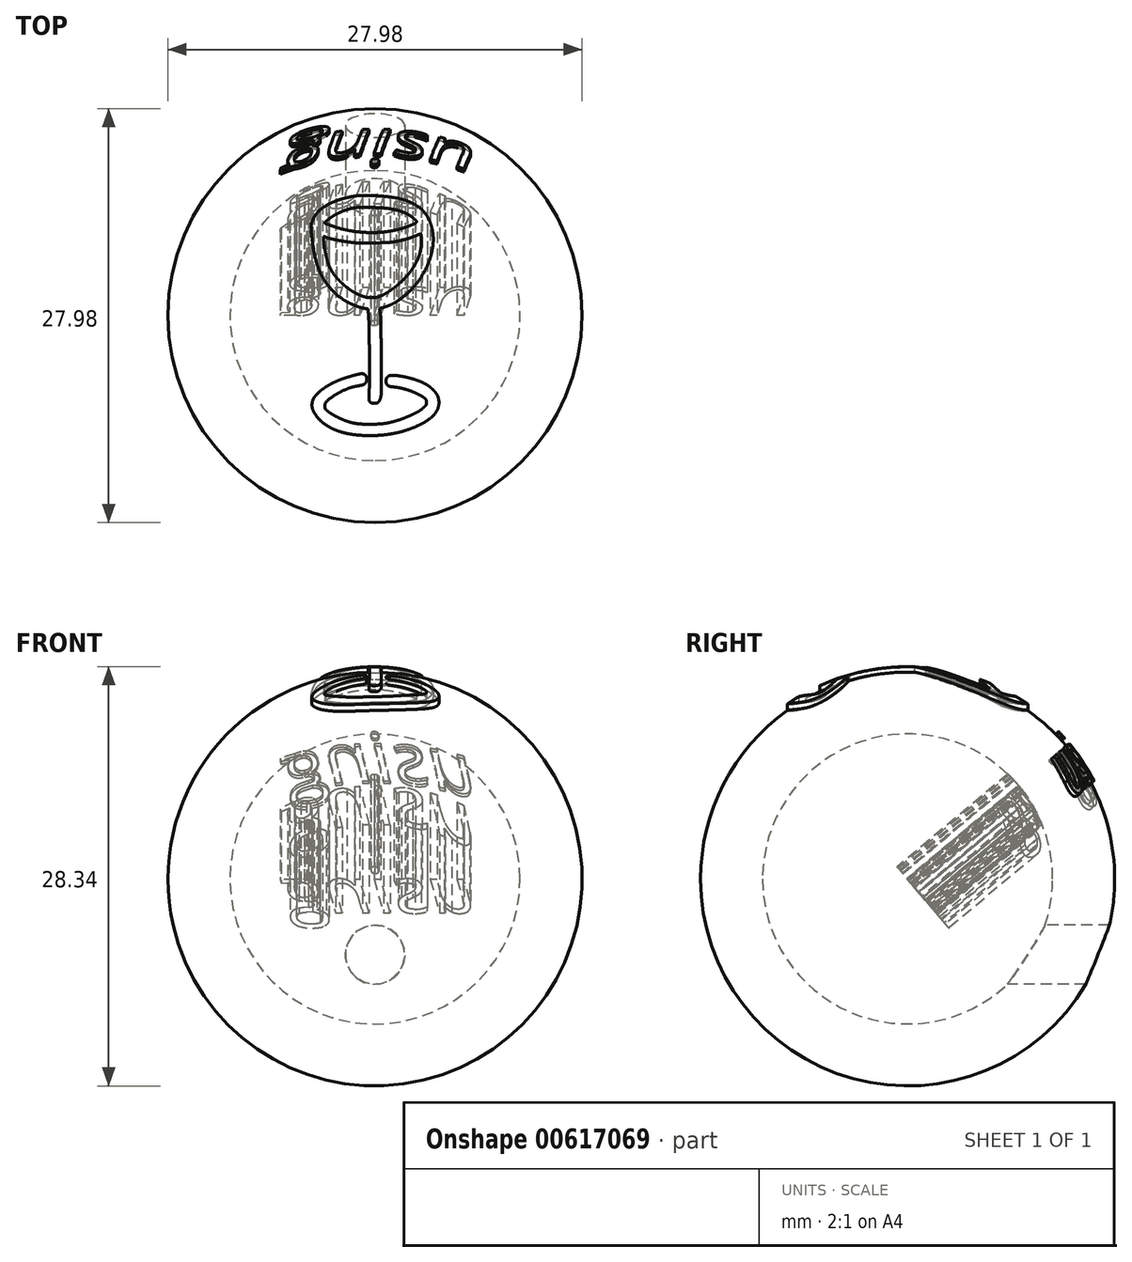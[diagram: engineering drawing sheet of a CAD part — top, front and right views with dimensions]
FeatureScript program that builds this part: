
annotation { "Feature Type Name" : "Feature", "Feature Type Description" : "" }
export const myFeature = defineFeature(function(context is Context, id is Id, definition is map)
    precondition{}
    {
        {
            var Q0;
            Q0=qCreatedBy(makeId("Top.planeOp"),FACE);
            var sketch = newSketch(context, id + "F0", { "sketchPlane" : qUnion([Q0])});
            skLineSegment(sketch, "E0", {"start": v(0, -10) * mm, "end": v(0, 10) * mm});
            skArc(sketch, "E1", {"start": v(0, 10) * mm, "mid": v(-10, 0) * mm, "end": v(0, -10) * mm});
            skSolve(sketch);
        }
        {
            var Q0;
            {var subQ0=sQuery(id+"F0.wireOp",EDGE,"E1");Q0=makeQuery(id+"F0.imprint","IMPRINT",FACE,{"disambiguationData":[TD([[makeQuery(id+"F0.imprint","IMPRINT",EDGE,{"derivedFrom":subQ0}),1.0]])]});}
            var Q1;
            Q1=sQuery(id+"F0.wireOp",EDGE,"E0");
            revolve(context, id + "F1", {"entities" : qUnion([Q0]), "axis" : qUnion([Q1]), "revolveType" : RevolveType.FULL});
        }
        {
            var Q0;
            Q0=makeQuery(id+"F1.opRevolve","SWEPT_BODY",BODY,{"disambiguationData":[OSD([sQuery(id+"F0.wireOp",EDGE,"E0"),sQuery(id+"F0.wireOp",EDGE,"E1")])]});
            var Q1;
            Q1=sQuery(id+"F0.wireOp",VERTEX,"NPe4G0ez-t7S9-9isL-QO5v-uuJu600mHcIT.center");
            var Q2;
            Q2=sQuery(id+"F0.wireOp",VERTEX,"E1.center");
            transform(context, id + "F2", {"entities" : qUnion([Q0]), "transformType" : TransformType.SCALE_UNIFORMLY, "scale" : 33.3, "scalePoint" : qUnion([Q2]), "makeCopy" : false});
        }
        {
            var Q0;
            Q0=qCreatedBy(makeId("Top.planeOp"),FACE);
            var sketch = newSketch(context, id + "F3", { "sketchPlane" : qUnion([Q0])});
            skArc(sketch, "E2", {"start": v(-28, 192.81) * mm, "mid": v(-31.38, 192.4) * mm, "end": v(-34.76, 191.86) * mm});
            skArc(sketch, "E3", {"start": v(-34.76, 191.86) * mm, "mid": v(-38.6, 191.14) * mm, "end": v(-42.43, 190.34) * mm});
            skArc(sketch, "E4", {"start": v(-42.43, 190.34) * mm, "mid": v(-46.3, 189.44) * mm, "end": v(-50.14, 188.46) * mm});
            skArc(sketch, "E5", {"start": v(-50.14, 188.46) * mm, "mid": v(-53.62, 187.47) * mm, "end": v(-57.07, 186.38) * mm});
            skArc(sketch, "E6", {"start": v(-57.07, 186.38) * mm, "mid": v(-64.8, 183.56) * mm, "end": v(-72.35, 180.29) * mm});
            skArc(sketch, "E7", {"start": v(-72.35, 180.29) * mm, "mid": v(-78.57, 177) * mm, "end": v(-84.46, 173.13) * mm});
            skArc(sketch, "E8", {"start": v(-84.46, 173.13) * mm, "mid": v(-89.14, 169.3) * mm, "end": v(-93.37, 164.97) * mm});
            skArc(sketch, "E9", {"start": v(-93.37, 164.97) * mm, "mid": v(-96.59, 160.63) * mm, "end": v(-99.08, 155.83) * mm});
            skArc(sketch, "E10", {"start": v(-99.08, 155.83) * mm, "mid": v(-99.5, 154.83) * mm, "end": v(-99.94, 153.82) * mm});
            skArc(sketch, "E11", {"start": v(-99.94, 153.82) * mm, "mid": v(-100.4, 152.79) * mm, "end": v(-100.85, 151.75) * mm});
            skArc(sketch, "E12", {"start": v(-100.85, 151.75) * mm, "mid": v(-101.26, 150.84) * mm, "end": v(-101.67, 149.92) * mm});
            skArc(sketch, "E13", {"start": v(-101.67, 149.92) * mm, "mid": v(-101.95, 149.32) * mm, "end": v(-102.24, 148.73) * mm});
            skArc(sketch, "E14", {"start": v(-102.24, 148.73) * mm, "mid": v(-102.57, 147.87) * mm, "end": v(-102.73, 146.96) * mm});
            skArc(sketch, "E15", {"start": v(-102.73, 146.96) * mm, "mid": v(-102.82, 145.41) * mm, "end": v(-102.85, 143.86) * mm});
            skArc(sketch, "E16", {"start": v(-102.85, 143.86) * mm, "mid": v(-102.8, 141.6) * mm, "end": v(-102.69, 139.34) * mm});
            skArc(sketch, "E17", {"start": v(-102.69, 139.34) * mm, "mid": v(-102.44, 135.94) * mm, "end": v(-102.17, 132.54) * mm});
            skArc(sketch, "E18", {"start": v(-102.17, 132.54) * mm, "mid": v(-100.04, 114.16) * mm, "end": v(-96.8, 95.94) * mm});
            skArc(sketch, "E19", {"start": v(-96.8, 95.94) * mm, "mid": v(-92.94, 81.56) * mm, "end": v(-87.47, 67.71) * mm});
            skArc(sketch, "E20", {"start": v(-87.47, 67.71) * mm, "mid": v(-81.13, 56.12) * mm, "end": v(-73.3, 45.49) * mm});
            skArc(sketch, "E21", {"start": v(-73.3, 45.49) * mm, "mid": v(-63.92, 35.71) * mm, "end": v(-53.4, 27.18) * mm});
            skArc(sketch, "E22", {"start": v(-53.4, 27.18) * mm, "mid": v(-49.24, 24.41) * mm, "end": v(-44.9, 21.92) * mm});
            skArc(sketch, "E23", {"start": v(-44.9, 21.92) * mm, "mid": v(-39.88, 19.4) * mm, "end": v(-34.74, 17.1) * mm});
            skArc(sketch, "E24", {"start": v(-34.74, 17.1) * mm, "mid": v(-29.55, 15.07) * mm, "end": v(-24.28, 13.28) * mm});
            skArc(sketch, "E25", {"start": v(-24.28, 13.28) * mm, "mid": v(-19.62, 12) * mm, "end": v(-14.89, 11.06) * mm});
            skLineSegment(sketch, "E26", {"start": v(-14.89, 11.06) * mm, "end": v(-11.28, 10.47) * mm});
            skLineSegment(sketch, "E27", {"start": v(-11.28, 10.47) * mm, "end": v(-10.56, 2.24) * mm});
            skArc(sketch, "E28", {"start": v(-10.56, 2.24) * mm, "mid": v(-9.95, -6.44) * mm, "end": v(-9.64, -15.14) * mm});
            skArc(sketch, "E29", {"start": v(-9.64, -15.14) * mm, "mid": v(-9.3, -35.9) * mm, "end": v(-9.02, -56.67) * mm});
            skArc(sketch, "E30", {"start": v(-9.02, -56.67) * mm, "mid": v(-8.82, -77.32) * mm, "end": v(-8.7, -97.97) * mm});
            skArc(sketch, "E31", {"start": v(-8.7, -97.97) * mm, "mid": v(-8.8, -108.17) * mm, "end": v(-9.18, -118.37) * mm});
            skArc(sketch, "E32", {"start": v(-9.18, -118.37) * mm, "mid": v(-9.47, -124.4) * mm, "end": v(-9.74, -130.44) * mm});
            skArc(sketch, "E33", {"start": v(-9.74, -130.44) * mm, "mid": v(-9.78, -132.57) * mm, "end": v(-9.7, -134.7) * mm});
            skArc(sketch, "E34", {"start": v(-9.7, -134.7) * mm, "mid": v(-9.52, -135.94) * mm, "end": v(-9.15, -137.13) * mm});
            skArc(sketch, "E35", {"start": v(-9.15, -137.13) * mm, "mid": v(-8.6, -138.18) * mm, "end": v(-7.87, -139.12) * mm});
            skArc(sketch, "E36", {"start": v(-7.87, -139.12) * mm, "mid": v(-7.27, -139.7) * mm, "end": v(-6.62, -140.22) * mm});
            skArc(sketch, "E37", {"start": v(-6.62, -140.22) * mm, "mid": v(-5.96, -140.63) * mm, "end": v(-5.26, -140.95) * mm});
            skArc(sketch, "E38", {"start": v(-5.26, -140.95) * mm, "mid": v(-4.48, -141.2) * mm, "end": v(-3.68, -141.36) * mm});
            skArc(sketch, "E39", {"start": v(-3.68, -141.36) * mm, "mid": v(-2.72, -141.46) * mm, "end": v(-1.75, -141.5) * mm});
            skArc(sketch, "E40", {"start": v(-1.75, -141.5) * mm, "mid": v(0, -141.42) * mm, "end": v(1.72, -141.18) * mm});
            skArc(sketch, "E41", {"start": v(1.72, -141.18) * mm, "mid": v(3.04, -140.82) * mm, "end": v(4.26, -140.22) * mm});
            skArc(sketch, "E42", {"start": v(4.26, -140.22) * mm, "mid": v(5.31, -139.43) * mm, "end": v(6.2, -138.45) * mm});
            skArc(sketch, "E43", {"start": v(6.2, -138.45) * mm, "mid": v(7.08, -137.1) * mm, "end": v(7.82, -135.66) * mm});
            skArc(sketch, "E44", {"start": v(7.82, -135.66) * mm, "mid": v(9.39, -130.88) * mm, "end": v(9.93, -125.87) * mm});
            skArc(sketch, "E45", {"start": v(9.93, -125.87) * mm, "mid": v(9.97, -95.78) * mm, "end": v(9.93, -65.68) * mm});
            skArc(sketch, "E46", {"start": v(9.93, -65.68) * mm, "mid": v(9.77, -36.7) * mm, "end": v(9.47, -7.73) * mm});
            skArc(sketch, "E47", {"start": v(9.47, -7.73) * mm, "mid": v(8.9, 0.7) * mm, "end": v(7.4, 9) * mm});
            skArc(sketch, "E48", {"start": v(7.4, 9) * mm, "mid": v(7.35, 9.57) * mm, "end": v(7.47, 10.13) * mm});
            skArc(sketch, "E49", {"start": v(7.47, 10.13) * mm, "mid": v(7.75, 10.61) * mm, "end": v(8.17, 10.99) * mm});
            skArc(sketch, "E50", {"start": v(8.17, 10.99) * mm, "mid": v(8.98, 11.43) * mm, "end": v(9.85, 11.77) * mm});
            skArc(sketch, "E51", {"start": v(9.85, 11.77) * mm, "mid": v(11.67, 12.35) * mm, "end": v(13.5, 12.9) * mm});
            skArc(sketch, "E52", {"start": v(13.5, 12.9) * mm, "mid": v(25.53, 17.38) * mm, "end": v(36.7, 23.67) * mm});
            skArc(sketch, "E53", {"start": v(36.7, 23.67) * mm, "mid": v(48.2, 32.34) * mm, "end": v(58.64, 42.23) * mm});
            skArc(sketch, "E54", {"start": v(58.64, 42.23) * mm, "mid": v(68.36, 53.67) * mm, "end": v(76.8, 66.08) * mm});
            skArc(sketch, "E55", {"start": v(76.8, 66.08) * mm, "mid": v(83.57, 78.94) * mm, "end": v(88.8, 92.5) * mm});
            skArc(sketch, "E56", {"start": v(88.8, 92.5) * mm, "mid": v(91.23, 101.41) * mm, "end": v(92.9, 110.5) * mm});
            skArc(sketch, "E57", {"start": v(92.9, 110.5) * mm, "mid": v(93.67, 119.1) * mm, "end": v(93.55, 127.73) * mm});
            skArc(sketch, "E58", {"start": v(93.55, 127.73) * mm, "mid": v(92.56, 135.93) * mm, "end": v(90.68, 143.97) * mm});
            skArc(sketch, "E59", {"start": v(90.68, 143.97) * mm, "mid": v(87.96, 151.66) * mm, "end": v(84.4, 159) * mm});
            skArc(sketch, "E60", {"start": v(84.4, 159) * mm, "mid": v(80.6, 164.75) * mm, "end": v(75.97, 169.86) * mm});
            skArc(sketch, "E61", {"start": v(75.97, 169.86) * mm, "mid": v(70.26, 174.63) * mm, "end": v(64.02, 178.68) * mm});
            skArc(sketch, "E62", {"start": v(64.02, 178.68) * mm, "mid": v(56.48, 182.45) * mm, "end": v(48.6, 185.4) * mm});
            skArc(sketch, "E63", {"start": v(48.6, 185.4) * mm, "mid": v(39.26, 188) * mm, "end": v(29.76, 189.95) * mm});
            skArc(sketch, "E64", {"start": v(29.76, 189.95) * mm, "mid": v(23.24, 190.92) * mm, "end": v(16.69, 191.62) * mm});
            skArc(sketch, "E65", {"start": v(16.69, 191.62) * mm, "mid": v(8.13, 192.28) * mm, "end": v(-0.44, 192.79) * mm});
            skArc(sketch, "E66", {"start": v(-0.44, 192.79) * mm, "mid": v(-8.76, 193.13) * mm, "end": v(-17.1, 193.32) * mm});
            skArc(sketch, "E67", {"start": v(-17.1, 193.32) * mm, "mid": v(-22.55, 193.23) * mm, "end": v(-28, 192.81) * mm});
            skArc(sketch, "E68", {"start": v(23, 172) * mm, "mid": v(27.27, 171.24) * mm, "end": v(31.52, 170.4) * mm});
            skArc(sketch, "E69", {"start": v(31.52, 170.4) * mm, "mid": v(34.9, 169.63) * mm, "end": v(38.25, 168.73) * mm});
            skArc(sketch, "E70", {"start": v(38.25, 168.73) * mm, "mid": v(41.28, 167.77) * mm, "end": v(44.27, 166.68) * mm});
            skArc(sketch, "E71", {"start": v(44.27, 166.68) * mm, "mid": v(47.43, 165.38) * mm, "end": v(50.56, 163.97) * mm});
            skArc(sketch, "E72", {"start": v(50.56, 163.97) * mm, "mid": v(53.44, 162.47) * mm, "end": v(56.2, 160.78) * mm});
            skArc(sketch, "E73", {"start": v(56.2, 160.78) * mm, "mid": v(59.05, 158.78) * mm, "end": v(61.78, 156.62) * mm});
            skArc(sketch, "E74", {"start": v(61.78, 156.62) * mm, "mid": v(64.08, 154.6) * mm, "end": v(66.28, 152.48) * mm});
            skArc(sketch, "E75", {"start": v(66.28, 152.48) * mm, "mid": v(66.84, 151.48) * mm, "end": v(66.79, 150.33) * mm});
            skArc(sketch, "E76", {"start": v(66.79, 150.33) * mm, "mid": v(66.12, 149.19) * mm, "end": v(65.05, 148.41) * mm});
            skArc(sketch, "E77", {"start": v(65.05, 148.41) * mm, "mid": v(60.8, 146.55) * mm, "end": v(56.5, 144.76) * mm});
            skArc(sketch, "E78", {"start": v(56.5, 144.76) * mm, "mid": v(51.74, 142.91) * mm, "end": v(46.93, 141.22) * mm});
            skArc(sketch, "E79", {"start": v(46.93, 141.22) * mm, "mid": v(42.34, 139.79) * mm, "end": v(37.7, 138.53) * mm});
            skArc(sketch, "E80", {"start": v(37.7, 138.53) * mm, "mid": v(24.83, 135.84) * mm, "end": v(11.79, 134.2) * mm});
            skArc(sketch, "E81", {"start": v(11.79, 134.2) * mm, "mid": v(-2.07, 133.48) * mm, "end": v(-15.94, 133.71) * mm});
            skArc(sketch, "E82", {"start": v(-15.94, 133.71) * mm, "mid": v(-29.73, 134.9) * mm, "end": v(-43.4, 137.01) * mm});
            skArc(sketch, "E83", {"start": v(-43.4, 137.01) * mm, "mid": v(-56.09, 139.97) * mm, "end": v(-68.5, 143.96) * mm});
            skArc(sketch, "E84", {"start": v(-68.5, 143.96) * mm, "mid": v(-70.45, 144.68) * mm, "end": v(-72.41, 145.4) * mm});
            skArc(sketch, "E85", {"start": v(-72.41, 145.4) * mm, "mid": v(-74.17, 146.03) * mm, "end": v(-75.92, 146.67) * mm});
            skArc(sketch, "E86", {"start": v(-75.92, 146.67) * mm, "mid": v(-77.4, 147.2) * mm, "end": v(-78.88, 147.74) * mm});
            skArc(sketch, "E87", {"start": v(-78.88, 147.74) * mm, "mid": v(-79.3, 147.9) * mm, "end": v(-79.74, 148.04) * mm});
            skArc(sketch, "E88", {"start": v(-79.74, 148.04) * mm, "mid": v(-80.25, 148.32) * mm, "end": v(-80.62, 148.77) * mm});
            skArc(sketch, "E89", {"start": v(-80.62, 148.77) * mm, "mid": v(-80.74, 149.28) * mm, "end": v(-80.58, 149.77) * mm});
            skArc(sketch, "E90", {"start": v(-80.58, 149.77) * mm, "mid": v(-79.94, 150.6) * mm, "end": v(-79.2, 151.33) * mm});
            skArc(sketch, "E91", {"start": v(-79.2, 151.33) * mm, "mid": v(-77.48, 152.74) * mm, "end": v(-75.74, 154.13) * mm});
            skArc(sketch, "E92", {"start": v(-75.74, 154.13) * mm, "mid": v(-70.76, 157.76) * mm, "end": v(-65.57, 161.08) * mm});
            skArc(sketch, "E93", {"start": v(-65.57, 161.08) * mm, "mid": v(-60.08, 164.12) * mm, "end": v(-54.43, 166.82) * mm});
            skArc(sketch, "E94", {"start": v(-54.43, 166.82) * mm, "mid": v(-48.77, 169.12) * mm, "end": v(-43, 171.06) * mm});
            skArc(sketch, "E95", {"start": v(-43, 171.06) * mm, "mid": v(-37.5, 172.49) * mm, "end": v(-31.93, 173.5) * mm});
            skArc(sketch, "E96", {"start": v(-31.93, 173.5) * mm, "mid": v(-27.17, 174) * mm, "end": v(-22.38, 174.16) * mm});
            skArc(sketch, "E97", {"start": v(-22.38, 174.16) * mm, "mid": v(-13.79, 174.1) * mm, "end": v(-5.2, 173.93) * mm});
            skArc(sketch, "E98", {"start": v(-5.2, 173.93) * mm, "mid": v(3.46, 173.63) * mm, "end": v(12.1, 173.2) * mm});
            skArc(sketch, "E99", {"start": v(12.1, 173.2) * mm, "mid": v(17.57, 172.75) * mm, "end": v(23, 172) * mm});
            skArc(sketch, "E100", {"start": v(74.45, 118.91) * mm, "mid": v(74.2, 112.9) * mm, "end": v(73.54, 106.92) * mm});
            skArc(sketch, "E101", {"start": v(73.54, 106.92) * mm, "mid": v(72.47, 101.46) * mm, "end": v(70.92, 96.12) * mm});
            skArc(sketch, "E102", {"start": v(70.92, 96.12) * mm, "mid": v(68.79, 90.64) * mm, "end": v(66.2, 85.35) * mm});
            skArc(sketch, "E103", {"start": v(66.2, 85.35) * mm, "mid": v(62.73, 79.3) * mm, "end": v(58.94, 73.4) * mm});
            skArc(sketch, "E104", {"start": v(58.94, 73.4) * mm, "mid": v(54.72, 67.67) * mm, "end": v(50.07, 62.26) * mm});
            skArc(sketch, "E105", {"start": v(50.07, 62.26) * mm, "mid": v(44.37, 56.43) * mm, "end": v(38.38, 50.9) * mm});
            skArc(sketch, "E106", {"start": v(38.38, 50.9) * mm, "mid": v(32.1, 45.67) * mm, "end": v(25.56, 40.76) * mm});
            skArc(sketch, "E107", {"start": v(25.56, 40.76) * mm, "mid": v(19.56, 36.81) * mm, "end": v(13.27, 33.33) * mm});
            skArc(sketch, "E108", {"start": v(13.27, 33.33) * mm, "mid": v(10.86, 32.14) * mm, "end": v(8.43, 31.02) * mm});
            skArc(sketch, "E109", {"start": v(8.43, 31.02) * mm, "mid": v(6.75, 30.34) * mm, "end": v(5.03, 29.79) * mm});
            skArc(sketch, "E110", {"start": v(5.03, 29.79) * mm, "mid": v(3.33, 29.38) * mm, "end": v(1.6, 29.12) * mm});
            skArc(sketch, "E111", {"start": v(1.6, 29.12) * mm, "mid": v(-0.81, 28.88) * mm, "end": v(-3.23, 28.72) * mm});
            skArc(sketch, "E112", {"start": v(-3.23, 28.72) * mm, "mid": v(-5.59, 28.63) * mm, "end": v(-7.95, 28.6) * mm});
            skArc(sketch, "E113", {"start": v(-7.95, 28.6) * mm, "mid": v(-9.7, 28.66) * mm, "end": v(-11.43, 28.84) * mm});
            skArc(sketch, "E114", {"start": v(-11.43, 28.84) * mm, "mid": v(-13.15, 29.14) * mm, "end": v(-14.86, 29.55) * mm});
            skArc(sketch, "E115", {"start": v(-14.86, 29.55) * mm, "mid": v(-17.14, 30.22) * mm, "end": v(-19.4, 30.94) * mm});
            skArc(sketch, "E116", {"start": v(-19.4, 30.94) * mm, "mid": v(-24.3, 32.77) * mm, "end": v(-29.04, 34.94) * mm});
            skArc(sketch, "E117", {"start": v(-29.04, 34.94) * mm, "mid": v(-33.85, 37.5) * mm, "end": v(-38.48, 40.37) * mm});
            skArc(sketch, "E118", {"start": v(-38.48, 40.37) * mm, "mid": v(-43.29, 43.72) * mm, "end": v(-47.9, 47.34) * mm});
            skArc(sketch, "E119", {"start": v(-47.9, 47.34) * mm, "mid": v(-52.76, 51.57) * mm, "end": v(-57.44, 56) * mm});
            skArc(sketch, "E120", {"start": v(-57.44, 56) * mm, "mid": v(-62.23, 61.17) * mm, "end": v(-66.53, 66.76) * mm});
            skArc(sketch, "E121", {"start": v(-66.53, 66.76) * mm, "mid": v(-70.15, 72.57) * mm, "end": v(-73.17, 78.7) * mm});
            skArc(sketch, "E122", {"start": v(-73.17, 78.7) * mm, "mid": v(-75.9, 85.84) * mm, "end": v(-77.98, 93.19) * mm});
            skArc(sketch, "E123", {"start": v(-77.98, 93.19) * mm, "mid": v(-79.95, 102.45) * mm, "end": v(-81.5, 111.79) * mm});
            skArc(sketch, "E124", {"start": v(-81.5, 111.79) * mm, "mid": v(-81.79, 113.84) * mm, "end": v(-82.06, 115.9) * mm});
            skArc(sketch, "E125", {"start": v(-82.06, 115.9) * mm, "mid": v(-82.3, 117.84) * mm, "end": v(-82.53, 119.8) * mm});
            skArc(sketch, "E126", {"start": v(-82.53, 119.8) * mm, "mid": v(-82.72, 121.44) * mm, "end": v(-82.89, 123.1) * mm});
            skArc(sketch, "E127", {"start": v(-82.89, 123.1) * mm, "mid": v(-82.95, 123.9) * mm, "end": v(-82.97, 124.7) * mm});
            skLineSegment(sketch, "E128", {"start": v(-82.97, 124.7) * mm, "end": v(-83, 127.4) * mm});
            skLineSegment(sketch, "E129", {"start": v(-83, 127.4) * mm, "end": v(-77.24, 125.41) * mm});
            skArc(sketch, "E130", {"start": v(-77.24, 125.41) * mm, "mid": v(-73.46, 124.22) * mm, "end": v(-69.61, 123.22) * mm});
            skArc(sketch, "E131", {"start": v(-69.61, 123.22) * mm, "mid": v(-64.09, 122) * mm, "end": v(-58.54, 120.88) * mm});
            skArc(sketch, "E132", {"start": v(-58.54, 120.88) * mm, "mid": v(-52.55, 119.8) * mm, "end": v(-46.55, 118.82) * mm});
            skArc(sketch, "E133", {"start": v(-46.55, 118.82) * mm, "mid": v(-41.1, 118.06) * mm, "end": v(-35.66, 117.44) * mm});
            skArc(sketch, "E134", {"start": v(-35.66, 117.44) * mm, "mid": v(-28.26, 116.87) * mm, "end": v(-20.84, 116.63) * mm});
            skArc(sketch, "E135", {"start": v(-20.84, 116.63) * mm, "mid": v(-10.4, 116.6) * mm, "end": v(0.05, 116.76) * mm});
            skArc(sketch, "E136", {"start": v(0.05, 116.76) * mm, "mid": v(10.3, 117.07) * mm, "end": v(20.54, 117.54) * mm});
            skArc(sketch, "E137", {"start": v(20.54, 117.54) * mm, "mid": v(26.8, 118.08) * mm, "end": v(33, 119) * mm});
            skArc(sketch, "E138", {"start": v(33, 119) * mm, "mid": v(37.48, 119.88) * mm, "end": v(41.92, 120.86) * mm});
            skArc(sketch, "E139", {"start": v(41.92, 120.86) * mm, "mid": v(46.33, 121.94) * mm, "end": v(50.71, 123.15) * mm});
            skArc(sketch, "E140", {"start": v(50.71, 123.15) * mm, "mid": v(54.81, 124.38) * mm, "end": v(58.87, 125.73) * mm});
            skArc(sketch, "E141", {"start": v(58.87, 125.73) * mm, "mid": v(62.4, 127.02) * mm, "end": v(65.87, 128.45) * mm});
            skArc(sketch, "E142", {"start": v(65.87, 128.45) * mm, "mid": v(67.17, 129.01) * mm, "end": v(68.48, 129.54) * mm});
            skArc(sketch, "E143", {"start": v(68.48, 129.54) * mm, "mid": v(69.66, 130) * mm, "end": v(70.85, 130.42) * mm});
            skArc(sketch, "E144", {"start": v(70.85, 130.42) * mm, "mid": v(71.84, 130.75) * mm, "end": v(72.84, 131.07) * mm});
            skArc(sketch, "E145", {"start": v(72.84, 131.07) * mm, "mid": v(73.17, 131.13) * mm, "end": v(73.5, 131.09) * mm});
            skArc(sketch, "E146", {"start": v(73.5, 131.09) * mm, "mid": v(73.8, 130.9) * mm, "end": v(73.94, 130.6) * mm});
            skArc(sketch, "E147", {"start": v(73.94, 130.6) * mm, "mid": v(74.09, 129.1) * mm, "end": v(74.22, 127.62) * mm});
            skArc(sketch, "E148", {"start": v(74.22, 127.62) * mm, "mid": v(74.34, 125.7) * mm, "end": v(74.4, 123.79) * mm});
            skArc(sketch, "E149", {"start": v(74.4, 123.79) * mm, "mid": v(74.45, 121.35) * mm, "end": v(74.45, 118.91) * mm});
            skArc(sketch, "E150", {"start": v(-34.65, -96.5) * mm, "mid": v(-43.47, -99) * mm, "end": v(-52.16, -101.92) * mm});
            skArc(sketch, "E151", {"start": v(-52.16, -101.92) * mm, "mid": v(-60, -105) * mm, "end": v(-67.65, -108.52) * mm});
            skArc(sketch, "E152", {"start": v(-67.65, -108.52) * mm, "mid": v(-74.33, -112.1) * mm, "end": v(-80.77, -116.1) * mm});
            skArc(sketch, "E153", {"start": v(-80.77, -116.1) * mm, "mid": v(-86.14, -120.06) * mm, "end": v(-91.13, -124.5) * mm});
            skArc(sketch, "E154", {"start": v(-91.13, -124.5) * mm, "mid": v(-93.26, -126.63) * mm, "end": v(-95.35, -128.8) * mm});
            skArc(sketch, "E155", {"start": v(-95.35, -128.8) * mm, "mid": v(-96.6, -130.2) * mm, "end": v(-97.73, -131.7) * mm});
            skArc(sketch, "E156", {"start": v(-97.73, -131.7) * mm, "mid": v(-98.56, -133.01) * mm, "end": v(-99.25, -134.4) * mm});
            skArc(sketch, "E157", {"start": v(-99.25, -134.4) * mm, "mid": v(-99.92, -136.08) * mm, "end": v(-100.48, -137.8) * mm});
            skArc(sketch, "E158", {"start": v(-100.48, -137.8) * mm, "mid": v(-101.1, -140.5) * mm, "end": v(-101.43, -143.24) * mm});
            skArc(sketch, "E159", {"start": v(-101.43, -143.24) * mm, "mid": v(-101.41, -145.8) * mm, "end": v(-101.04, -148.34) * mm});
            skArc(sketch, "E160", {"start": v(-101.04, -148.34) * mm, "mid": v(-100.3, -151.03) * mm, "end": v(-99.22, -153.6) * mm});
            skArc(sketch, "E161", {"start": v(-99.22, -153.6) * mm, "mid": v(-97.61, -156.62) * mm, "end": v(-95.8, -159.53) * mm});
            skArc(sketch, "E162", {"start": v(-95.8, -159.53) * mm, "mid": v(-89.92, -166.94) * mm, "end": v(-82.9, -173.28) * mm});
            skArc(sketch, "E163", {"start": v(-82.9, -173.28) * mm, "mid": v(-74.32, -179.02) * mm, "end": v(-65.07, -183.62) * mm});
            skArc(sketch, "E164", {"start": v(-65.07, -183.62) * mm, "mid": v(-54.02, -187.58) * mm, "end": v(-42.6, -190.32) * mm});
            skArc(sketch, "E165", {"start": v(-42.6, -190.32) * mm, "mid": v(-29.29, -192.24) * mm, "end": v(-15.88, -193.2) * mm});
            skArc(sketch, "E166", {"start": v(-15.88, -193.2) * mm, "mid": v(-3.6, -193.28) * mm, "end": v(8.67, -192.7) * mm});
            skArc(sketch, "E167", {"start": v(8.67, -192.7) * mm, "mid": v(20.3, -191.45) * mm, "end": v(31.83, -189.47) * mm});
            skArc(sketch, "E168", {"start": v(31.83, -189.47) * mm, "mid": v(42.82, -186.85) * mm, "end": v(53.62, -183.51) * mm});
            skArc(sketch, "E169", {"start": v(53.62, -183.51) * mm, "mid": v(64, -179.52) * mm, "end": v(74.07, -174.83) * mm});
            skArc(sketch, "E170", {"start": v(74.07, -174.83) * mm, "mid": v(81.9, -170.36) * mm, "end": v(89.25, -165.16) * mm});
            skArc(sketch, "E171", {"start": v(89.25, -165.16) * mm, "mid": v(94.55, -160.17) * mm, "end": v(98.88, -154.31) * mm});
            skArc(sketch, "E172", {"start": v(98.88, -154.31) * mm, "mid": v(101.48, -148.67) * mm, "end": v(102.73, -142.58) * mm});
            skArc(sketch, "E173", {"start": v(102.73, -142.58) * mm, "mid": v(102.6, -136.36) * mm, "end": v(101.06, -130.32) * mm});
            skArc(sketch, "E174", {"start": v(101.06, -130.32) * mm, "mid": v(99.8, -127.56) * mm, "end": v(98.15, -125) * mm});
            skArc(sketch, "E175", {"start": v(98.15, -125) * mm, "mid": v(95.8, -122.07) * mm, "end": v(93.23, -119.32) * mm});
            skArc(sketch, "E176", {"start": v(93.23, -119.32) * mm, "mid": v(90.25, -116.55) * mm, "end": v(87.08, -114) * mm});
            skArc(sketch, "E177", {"start": v(87.08, -114) * mm, "mid": v(83.81, -111.76) * mm, "end": v(80.39, -109.77) * mm});
            skArc(sketch, "E178", {"start": v(80.39, -109.77) * mm, "mid": v(74.8, -107.06) * mm, "end": v(69.03, -104.76) * mm});
            skArc(sketch, "E179", {"start": v(69.03, -104.76) * mm, "mid": v(62.06, -102.45) * mm, "end": v(55, -100.46) * mm});
            skArc(sketch, "E180", {"start": v(55, -100.46) * mm, "mid": v(47.95, -98.8) * mm, "end": v(40.82, -97.46) * mm});
            skArc(sketch, "E181", {"start": v(40.82, -97.46) * mm, "mid": v(34.96, -96.74) * mm, "end": v(29.05, -96.5) * mm});
            skArc(sketch, "E182", {"start": v(29.05, -96.5) * mm, "mid": v(27.14, -96.52) * mm, "end": v(25.23, -96.58) * mm});
            skArc(sketch, "E183", {"start": v(25.23, -96.58) * mm, "mid": v(24.15, -96.7) * mm, "end": v(23.09, -96.93) * mm});
            skArc(sketch, "E184", {"start": v(23.09, -96.93) * mm, "mid": v(22.28, -97.24) * mm, "end": v(21.53, -97.68) * mm});
            skArc(sketch, "E185", {"start": v(21.53, -97.68) * mm, "mid": v(20.7, -98.32) * mm, "end": v(19.96, -99.05) * mm});
            skArc(sketch, "E186", {"start": v(19.96, -99.05) * mm, "mid": v(18.9, -100.41) * mm, "end": v(18.15, -101.96) * mm});
            skArc(sketch, "E187", {"start": v(18.15, -101.96) * mm, "mid": v(17.67, -103.68) * mm, "end": v(17.5, -105.46) * mm});
            skArc(sketch, "E188", {"start": v(17.5, -105.46) * mm, "mid": v(17.64, -107.23) * mm, "end": v(18.1, -108.95) * mm});
            skArc(sketch, "E189", {"start": v(18.1, -108.95) * mm, "mid": v(18.82, -110.48) * mm, "end": v(19.85, -111.83) * mm});
            skArc(sketch, "E190", {"start": v(19.85, -111.83) * mm, "mid": v(20.58, -112.51) * mm, "end": v(21.4, -113.1) * mm});
            skArc(sketch, "E191", {"start": v(21.4, -113.1) * mm, "mid": v(22.26, -113.58) * mm, "end": v(23.18, -113.94) * mm});
            skArc(sketch, "E192", {"start": v(23.18, -113.94) * mm, "mid": v(24.43, -114.28) * mm, "end": v(25.7, -114.51) * mm});
            skArc(sketch, "E193", {"start": v(25.7, -114.51) * mm, "mid": v(27.76, -114.77) * mm, "end": v(29.83, -114.99) * mm});
            skArc(sketch, "E194", {"start": v(29.83, -114.99) * mm, "mid": v(34.38, -115.52) * mm, "end": v(38.9, -116.3) * mm});
            skArc(sketch, "E195", {"start": v(38.9, -116.3) * mm, "mid": v(43.66, -117.33) * mm, "end": v(48.37, -118.56) * mm});
            skArc(sketch, "E196", {"start": v(48.37, -118.56) * mm, "mid": v(53.13, -120.02) * mm, "end": v(57.83, -121.68) * mm});
            skArc(sketch, "E197", {"start": v(57.83, -121.68) * mm, "mid": v(62.38, -123.5) * mm, "end": v(66.85, -125.51) * mm});
            skArc(sketch, "E198", {"start": v(66.85, -125.51) * mm, "mid": v(71.1, -127.61) * mm, "end": v(75.29, -129.81) * mm});
            skArc(sketch, "E199", {"start": v(75.29, -129.81) * mm, "mid": v(77.66, -131.27) * mm, "end": v(79.85, -133) * mm});
            skArc(sketch, "E200", {"start": v(79.85, -133) * mm, "mid": v(81.17, -134.41) * mm, "end": v(82.18, -136.07) * mm});
            skArc(sketch, "E201", {"start": v(82.18, -136.07) * mm, "mid": v(82.8, -137.85) * mm, "end": v(83, -139.72) * mm});
            skArc(sketch, "E202", {"start": v(83, -139.72) * mm, "mid": v(82.96, -140.83) * mm, "end": v(82.8, -141.93) * mm});
            skArc(sketch, "E203", {"start": v(82.8, -141.93) * mm, "mid": v(82.56, -142.82) * mm, "end": v(82.18, -143.67) * mm});
            skArc(sketch, "E204", {"start": v(82.18, -143.67) * mm, "mid": v(81.6, -144.6) * mm, "end": v(80.91, -145.45) * mm});
            skArc(sketch, "E205", {"start": v(80.91, -145.45) * mm, "mid": v(79.73, -146.72) * mm, "end": v(78.5, -147.95) * mm});
            skArc(sketch, "E206", {"start": v(78.5, -147.95) * mm, "mid": v(74.22, -151.58) * mm, "end": v(69.49, -154.6) * mm});
            skArc(sketch, "E207", {"start": v(69.49, -154.6) * mm, "mid": v(62.23, -158.37) * mm, "end": v(54.81, -161.8) * mm});
            skArc(sketch, "E208", {"start": v(54.81, -161.8) * mm, "mid": v(46.47, -165.2) * mm, "end": v(37.99, -168.23) * mm});
            skArc(sketch, "E209", {"start": v(37.99, -168.23) * mm, "mid": v(29.88, -170.67) * mm, "end": v(21.66, -172.67) * mm});
            skArc(sketch, "E210", {"start": v(21.66, -172.67) * mm, "mid": v(15.6, -173.75) * mm, "end": v(9.47, -174.4) * mm});
            skArc(sketch, "E211", {"start": v(9.47, -174.4) * mm, "mid": v(1.44, -174.86) * mm, "end": v(-6.6, -175.06) * mm});
            skArc(sketch, "E212", {"start": v(-6.6, -175.06) * mm, "mid": v(-14.57, -175) * mm, "end": v(-22.52, -174.7) * mm});
            skArc(sketch, "E213", {"start": v(-22.52, -174.7) * mm, "mid": v(-28.28, -174.16) * mm, "end": v(-33.98, -173.17) * mm});
            skArc(sketch, "E214", {"start": v(-33.98, -173.17) * mm, "mid": v(-42.09, -171.07) * mm, "end": v(-50, -168.32) * mm});
            skArc(sketch, "E215", {"start": v(-50, -168.32) * mm, "mid": v(-57.95, -164.86) * mm, "end": v(-65.6, -160.83) * mm});
            skArc(sketch, "E216", {"start": v(-65.6, -160.83) * mm, "mid": v(-71.87, -156.93) * mm, "end": v(-77.84, -152.6) * mm});
            skArc(sketch, "E217", {"start": v(-77.84, -152.6) * mm, "mid": v(-80.16, -149.75) * mm, "end": v(-81, -146.16) * mm});
            skArc(sketch, "E218", {"start": v(-81, -146.16) * mm, "mid": v(-79.94, -141.3) * mm, "end": v(-76.96, -137.33) * mm});
            skArc(sketch, "E219", {"start": v(-76.96, -137.33) * mm, "mid": v(-70, -131.79) * mm, "end": v(-62.58, -126.88) * mm});
            skArc(sketch, "E220", {"start": v(-62.58, -126.88) * mm, "mid": v(-53.6, -121.99) * mm, "end": v(-44.23, -117.89) * mm});
            skArc(sketch, "E221", {"start": v(-44.23, -117.89) * mm, "mid": v(-35.24, -114.97) * mm, "end": v(-26, -113.05) * mm});
            skArc(sketch, "E222", {"start": v(-26, -113.05) * mm, "mid": v(-23.72, -112.66) * mm, "end": v(-21.46, -112.16) * mm});
            skArc(sketch, "E223", {"start": v(-21.46, -112.16) * mm, "mid": v(-19.83, -111.67) * mm, "end": v(-18.26, -111) * mm});
            skArc(sketch, "E224", {"start": v(-18.26, -111) * mm, "mid": v(-17.07, -110.31) * mm, "end": v(-16, -109.46) * mm});
            skArc(sketch, "E225", {"start": v(-16, -109.46) * mm, "mid": v(-15.14, -108.5) * mm, "end": v(-14.44, -107.4) * mm});
            skArc(sketch, "E226", {"start": v(-14.44, -107.4) * mm, "mid": v(-13.76, -105.86) * mm, "end": v(-13.28, -104.24) * mm});
            skArc(sketch, "E227", {"start": v(-13.28, -104.24) * mm, "mid": v(-13.05, -102.7) * mm, "end": v(-13.06, -101.14) * mm});
            skArc(sketch, "E228", {"start": v(-13.06, -101.14) * mm, "mid": v(-13.3, -99.7) * mm, "end": v(-13.8, -98.31) * mm});
            skArc(sketch, "E229", {"start": v(-13.8, -98.31) * mm, "mid": v(-14.52, -97.06) * mm, "end": v(-15.45, -95.95) * mm});
            skArc(sketch, "E230", {"start": v(-15.45, -95.95) * mm, "mid": v(-16.65, -94.96) * mm, "end": v(-18.03, -94.24) * mm});
            skArc(sketch, "E231", {"start": v(-18.03, -94.24) * mm, "mid": v(-19.5, -93.8) * mm, "end": v(-21.04, -93.7) * mm});
            skArc(sketch, "E232", {"start": v(-21.04, -93.7) * mm, "mid": v(-23.35, -93.87) * mm, "end": v(-25.63, -94.28) * mm});
            skArc(sketch, "E233", {"start": v(-25.63, -94.28) * mm, "mid": v(-30.15, -95.35) * mm, "end": v(-34.65, -96.5) * mm});
            skArc(sketch, "E234", {"start": v(46.5, 109.42) * mm, "mid": v(40.62, 107.91) * mm, "end": v(34.69, 106.57) * mm});
            skArc(sketch, "E235", {"start": v(34.69, 106.57) * mm, "mid": v(29.15, 105.5) * mm, "end": v(23.57, 104.64) * mm});
            skArc(sketch, "E236", {"start": v(23.57, 104.64) * mm, "mid": v(17.7, 103.94) * mm, "end": v(11.79, 103.43) * mm});
            skArc(sketch, "E237", {"start": v(11.79, 103.43) * mm, "mid": v(4.84, 103.03) * mm, "end": v(-2.12, 102.78) * mm});
            skArc(sketch, "E238", {"start": v(-2.12, 102.78) * mm, "mid": v(-9.27, 102.65) * mm, "end": v(-16.41, 102.65) * mm});
            skArc(sketch, "E239", {"start": v(-16.41, 102.65) * mm, "mid": v(-22.2, 102.8) * mm, "end": v(-28, 103.15) * mm});
            skArc(sketch, "E240", {"start": v(-28, 103.15) * mm, "mid": v(-33.66, 103.68) * mm, "end": v(-39.3, 104.4) * mm});
            skArc(sketch, "E241", {"start": v(-39.3, 104.4) * mm, "mid": v(-46.04, 105.44) * mm, "end": v(-52.75, 106.63) * mm});
            skArc(sketch, "E242", {"start": v(-52.75, 106.63) * mm, "mid": v(-56.1, 107.24) * mm, "end": v(-59.46, 107.82) * mm});
            skArc(sketch, "E243", {"start": v(-59.46, 107.82) * mm, "mid": v(-61.02, 108.03) * mm, "end": v(-62.6, 108.15) * mm});
            skArc(sketch, "E244", {"start": v(-62.6, 108.15) * mm, "mid": v(-63.62, 108.12) * mm, "end": v(-64.62, 107.94) * mm});
            skArc(sketch, "E245", {"start": v(-64.62, 107.94) * mm, "mid": v(-65.53, 107.63) * mm, "end": v(-66.38, 107.17) * mm});
            skArc(sketch, "E246", {"start": v(-66.38, 107.17) * mm, "mid": v(-67.47, 106.28) * mm, "end": v(-68.35, 105.2) * mm});
            skArc(sketch, "E247", {"start": v(-68.35, 105.2) * mm, "mid": v(-68.99, 103.94) * mm, "end": v(-69.35, 102.58) * mm});
            skArc(sketch, "E248", {"start": v(-69.35, 102.58) * mm, "mid": v(-69.51, 100.78) * mm, "end": v(-69.41, 98.99) * mm});
            skArc(sketch, "E249", {"start": v(-69.41, 98.99) * mm, "mid": v(-69.03, 96.45) * mm, "end": v(-68.51, 93.93) * mm});
            skArc(sketch, "E250", {"start": v(-68.51, 93.93) * mm, "mid": v(-65.52, 84.43) * mm, "end": v(-61.12, 75.5) * mm});
            skArc(sketch, "E251", {"start": v(-61.12, 75.5) * mm, "mid": v(-55.22, 66.9) * mm, "end": v(-48.23, 59.16) * mm});
            skArc(sketch, "E252", {"start": v(-48.23, 59.16) * mm, "mid": v(-40.25, 52.4) * mm, "end": v(-31.44, 46.78) * mm});
            skArc(sketch, "E253", {"start": v(-31.44, 46.78) * mm, "mid": v(-22.3, 42.62) * mm, "end": v(-12.64, 39.88) * mm});
            skArc(sketch, "E254", {"start": v(-12.64, 39.88) * mm, "mid": v(-8.94, 39.25) * mm, "end": v(-5.2, 38.86) * mm});
            skArc(sketch, "E255", {"start": v(-5.2, 38.86) * mm, "mid": v(-2.07, 38.8) * mm, "end": v(1.05, 39.1) * mm});
            skArc(sketch, "E256", {"start": v(1.05, 39.1) * mm, "mid": v(4.22, 39.76) * mm, "end": v(7.3, 40.74) * mm});
            skArc(sketch, "E257", {"start": v(7.3, 40.74) * mm, "mid": v(11.1, 42.3) * mm, "end": v(14.81, 44.05) * mm});
            skArc(sketch, "E258", {"start": v(14.81, 44.05) * mm, "mid": v(21.86, 48.1) * mm, "end": v(28.42, 52.91) * mm});
            skArc(sketch, "E259", {"start": v(28.42, 52.91) * mm, "mid": v(35.27, 58.99) * mm, "end": v(41.62, 65.57) * mm});
            skArc(sketch, "E260", {"start": v(41.62, 65.57) * mm, "mid": v(47.4, 72.58) * mm, "end": v(52.6, 80.02) * mm});
            skArc(sketch, "E261", {"start": v(52.6, 80.02) * mm, "mid": v(56.5, 86.92) * mm, "end": v(59.58, 94.23) * mm});
            skArc(sketch, "E262", {"start": v(59.58, 94.23) * mm, "mid": v(60.52, 97.08) * mm, "end": v(61.37, 99.97) * mm});
            skArc(sketch, "E263", {"start": v(61.37, 99.97) * mm, "mid": v(61.74, 101.84) * mm, "end": v(61.87, 103.74) * mm});
            skArc(sketch, "E264", {"start": v(61.87, 103.74) * mm, "mid": v(61.72, 105.18) * mm, "end": v(61.27, 106.56) * mm});
            skArc(sketch, "E265", {"start": v(61.27, 106.56) * mm, "mid": v(60.52, 107.88) * mm, "end": v(59.55, 109.05) * mm});
            skArc(sketch, "E266", {"start": v(59.55, 109.05) * mm, "mid": v(58.55, 109.93) * mm, "end": v(57.45, 110.68) * mm});
            skArc(sketch, "E267", {"start": v(57.45, 110.68) * mm, "mid": v(56.48, 111.1) * mm, "end": v(55.44, 111.26) * mm});
            skArc(sketch, "E268", {"start": v(55.44, 111.26) * mm, "mid": v(54, 111.2) * mm, "end": v(52.58, 110.97) * mm});
            skArc(sketch, "E269", {"start": v(52.58, 110.97) * mm, "mid": v(49.54, 110.22) * mm, "end": v(46.5, 109.42) * mm});
            skSolve(sketch);
        }
        {
            var Q0;
            Q0=qSketchRegion(id+"F3",true);
            var Q1;
            Q1=sQuery(id+"F3.wireOp",EDGE,"c928f899-12af-4b01-b412-b3b7da3d830f");
            var Q2;
            Q2=sQuery(id+"F3.wireOp",EDGE,"b69f99c7-a6d0-4d1b-8752-9e82ab4c99ec");
            extrude(context, id + "F4", {"entities" : qUnion([Q0]), "operationType" : NewBodyOperationType.ADD, "surfaceEntities" : qUnion([Q1, Q2]), "depth" : 350 * mm});
        }
        {
            var Q0;
            Q0=makeQuery(id+"F4.opExtrude","SWEPT_BODY",BODY,{"disambiguationData":[OSD([sQuery(id+"F3.wireOp",EDGE,"15c6da4e-992d-4824-9d20-70d2d6be9970"),sQuery(id+"F3.wireOp",EDGE,"268c69ec-46be-456f-85eb-69decc32fe39"),sQuery(id+"F3.wireOp",EDGE,"1d386307-6059-4203-bca6-0c1cec3c82e1"),sQuery(id+"F3.wireOp",EDGE,"7d7c66d2-f869-427f-806b-ad436cacd60e"),sQuery(id+"F3.wireOp",EDGE,"1db91850-860e-493f-a3af-7a0f3f1512ae"),sQuery(id+"F3.wireOp",EDGE,"2c65f23b-9f03-4f6f-ab37-de452af29e3c"),sQuery(id+"F3.wireOp",EDGE,"ba006cbc-bbd7-44d9-84cc-9cde0967c280"),sQuery(id+"F3.wireOp",EDGE,"ae950208-c781-4a25-8fcf-ffe59b9085ff"),sQuery(id+"F3.wireOp",EDGE,"3cce0944-c62d-4831-9b9d-d1a418d328b4"),sQuery(id+"F3.wireOp",EDGE,"9edc5e7d-16c0-40c4-98ad-6b91d5df0e78"),sQuery(id+"F3.wireOp",EDGE,"aa452f44-44a2-4c64-bff5-a2a639df00db"),sQuery(id+"F3.wireOp",EDGE,"16259f99-ce20-4b7b-81e1-fa0909c03eb4"),sQuery(id+"F3.wireOp",EDGE,"79895566-a943-429d-b257-d76af3645bdf"),sQuery(id+"F3.wireOp",EDGE,"a85490ef-f17e-45c8-b92b-28215162778a"),sQuery(id+"F3.wireOp",EDGE,"322f1036-a6fd-4992-ab69-5919540af7a6"),sQuery(id+"F3.wireOp",EDGE,"0a87ff38-4ab4-4140-b3c3-2d7501d9f3b1"),sQuery(id+"F3.wireOp",EDGE,"a6e7bdf2-ef3e-49d4-9b3c-e34f5a41e0c4"),sQuery(id+"F3.wireOp",EDGE,"3e588790-576f-47c1-9730-f5e27fa1e8f9"),sQuery(id+"F3.wireOp",EDGE,"ce3739ef-15fd-4754-ad9c-ccf511a9a8fb"),sQuery(id+"F3.wireOp",EDGE,"201134a3-66f3-4a3f-aa9b-76948966efc0"),sQuery(id+"F3.wireOp",EDGE,"65b511ea-0759-428d-8070-88e1f521d8ea"),sQuery(id+"F3.wireOp",EDGE,"c37cddb6-5cf8-4891-aff4-7191a72080b9"),sQuery(id+"F3.wireOp",EDGE,"52a43dbd-e952-43e1-be3d-d70e107260e6"),sQuery(id+"F3.wireOp",EDGE,"08c1271f-f5c3-4f26-be27-7f5e21217dff"),sQuery(id+"F3.wireOp",EDGE,"59a09f58-0503-4180-962a-e04db21f0da8"),sQuery(id+"F3.wireOp",EDGE,"e56a4626-e956-42c3-bb5d-cd9dae1ca801"),sQuery(id+"F3.wireOp",EDGE,"5ff5d55f-af90-49eb-8040-353101557de8"),sQuery(id+"F3.wireOp",EDGE,"0ed7430b-e164-4f56-8af9-4534524aa7c0"),sQuery(id+"F3.wireOp",EDGE,"b5610a6e-b6bb-43e3-9a8d-d3d7c5f0098b"),sQuery(id+"F3.wireOp",EDGE,"1d417af8-88ad-47c2-a4e2-6fec82bd6695"),sQuery(id+"F3.wireOp",EDGE,"778ae99a-956a-4ddb-8078-d9bc57f9fc8e"),sQuery(id+"F3.wireOp",EDGE,"5b19af09-f144-446e-9dfa-8766819c9efd"),sQuery(id+"F3.wireOp",EDGE,"028339f6-0475-4a57-af8d-550e32ad7466"),sQuery(id+"F3.wireOp",EDGE,"d5ae35b6-d210-433a-92c8-e92622696872"),sQuery(id+"F3.wireOp",EDGE,"16a2e606-2caa-4876-9ffa-8f08c4ff3a37"),sQuery(id+"F3.wireOp",EDGE,"5b90b144-be56-4de7-a9dd-c1e0336acbe3"),sQuery(id+"F3.wireOp",EDGE,"5912d126-c5fc-41e4-bfb8-b4fefc52ca72"),sQuery(id+"F3.wireOp",EDGE,"2e96ce95-bd3e-4f27-a7f8-b62cf5efe954"),sQuery(id+"F3.wireOp",EDGE,"ecb4e259-1207-4dd0-bc3c-87c6506cc3a5"),sQuery(id+"F3.wireOp",EDGE,"105fb72e-4d79-4204-af2f-b3b26f5eb8d1"),sQuery(id+"F3.wireOp",EDGE,"fa59b598-df54-48c6-bb8f-c5f7618c69d0"),sQuery(id+"F3.wireOp",EDGE,"a6beef0d-f124-47ac-b957-e6cd3057a354"),sQuery(id+"F3.wireOp",EDGE,"7c3eaf53-dcb7-43b1-ad18-80ff953eb59e"),sQuery(id+"F3.wireOp",EDGE,"281fe206-104f-408f-94b6-be79f12604c9")])]});
            var Q1;
            Q1=makeQuery(id+"F4.opExtrude","SWEPT_BODY",BODY,{"disambiguationData":[OSD([sQuery(id+"F3.wireOp",EDGE,"58f6206a-5554-41d4-8cf7-6e0b4724a469"),sQuery(id+"F3.wireOp",EDGE,"85dabe77-b6aa-43d5-a519-64383616f71e"),sQuery(id+"F3.wireOp",EDGE,"4b679fe6-9e11-497d-b8fd-14ca14e49ddd"),sQuery(id+"F3.wireOp",EDGE,"51de25f6-d59e-4805-a327-1fd7e38869c8"),sQuery(id+"F3.wireOp",EDGE,"d47977fb-70d3-4df8-bc35-66fcc0e556e0"),sQuery(id+"F3.wireOp",EDGE,"235006b0-8f14-4ca2-82f0-f96b6b8c4766"),sQuery(id+"F3.wireOp",EDGE,"0fc7acd6-1c1d-47a8-ba12-62eb658d35ca"),sQuery(id+"F3.wireOp",EDGE,"883fa5e3-ca4c-4ce6-a249-4debf538fe24"),sQuery(id+"F3.wireOp",EDGE,"1da09ed1-22d9-43a1-a655-8acff5d61309"),sQuery(id+"F3.wireOp",EDGE,"32654a82-a09a-444f-bf73-45f818f0f235"),sQuery(id+"F3.wireOp",EDGE,"a398fd80-a0a9-4724-ba0e-1a7a000baa92"),sQuery(id+"F3.wireOp",EDGE,"f39f97c8-53f5-4046-9905-b28daecd4f10"),sQuery(id+"F3.wireOp",EDGE,"2484d883-0ec2-4c7d-9023-165ebbef226c"),sQuery(id+"F3.wireOp",EDGE,"f026d96f-3d32-4113-a1c9-3545f5cdbe4a"),sQuery(id+"F3.wireOp",EDGE,"974fee18-719e-4620-aace-d3676da2011b"),sQuery(id+"F3.wireOp",EDGE,"0c5766d2-a026-45af-bffd-0d1f783d5157"),sQuery(id+"F3.wireOp",EDGE,"5da13fee-9c04-45d8-805f-c7a03dde2383"),sQuery(id+"F3.wireOp",EDGE,"dbea32a3-85bd-4957-aef2-b6fe64a02f6b"),sQuery(id+"F3.wireOp",EDGE,"fba134ea-bf40-4191-ad8f-cc6b2b040a97"),sQuery(id+"F3.wireOp",EDGE,"0c19e200-7cd5-4fcb-83ed-261bd7936bc7"),sQuery(id+"F3.wireOp",EDGE,"246b843b-ea86-44e5-9cb9-335e6677b61d"),sQuery(id+"F3.wireOp",EDGE,"c1b3c9bc-1eb4-4c9b-99c8-0cebed89395a"),sQuery(id+"F3.wireOp",EDGE,"f93eebc3-1447-4029-8362-91325193ac2b"),sQuery(id+"F3.wireOp",EDGE,"bf86b12d-53a9-4c19-abaa-b1e658933ceb"),sQuery(id+"F3.wireOp",EDGE,"89646a71-1a60-4e14-b80a-74fb601d0855"),sQuery(id+"F3.wireOp",EDGE,"7b03dcde-0a52-4f3c-80e9-110d1d805e93"),sQuery(id+"F3.wireOp",EDGE,"83e8d1f3-8820-485b-8b6d-3ecd79124883"),sQuery(id+"F3.wireOp",EDGE,"ec7b56eb-ca95-44fd-a774-e9b7f9d3f50d"),sQuery(id+"F3.wireOp",EDGE,"31861aa6-cfd1-43ce-a7c5-bacfb7e2a30f"),sQuery(id+"F3.wireOp",EDGE,"fa3de647-1dd9-4141-982b-74ae8d07851d"),sQuery(id+"F3.wireOp",EDGE,"75d7c1c5-761c-4178-bfd4-4f469045899b"),sQuery(id+"F3.wireOp",EDGE,"4b3d7518-bd5d-4ecc-b2c5-d8dd665de4f4"),sQuery(id+"F3.wireOp",EDGE,"3be2682d-01bd-4f31-9cde-9df16a01e4a9"),sQuery(id+"F3.wireOp",EDGE,"72d3c7a9-2794-46eb-9b0d-6c526cc1b9a3"),sQuery(id+"F3.wireOp",EDGE,"0137e336-6b26-4f8d-b9ad-47ce1aa9eb31"),sQuery(id+"F3.wireOp",EDGE,"96000e4a-2d86-4b9f-af7d-a1c875cc048c"),sQuery(id+"F3.wireOp",EDGE,"139c5a79-9c0f-4e15-b57f-4c09662495a3"),sQuery(id+"F3.wireOp",EDGE,"8ea04d8b-b3da-46bb-9742-d8cba6b23bda"),sQuery(id+"F3.wireOp",EDGE,"b352b580-467e-481c-88ac-6217b8462947"),sQuery(id+"F3.wireOp",EDGE,"2503a493-1722-4539-8d54-7329fc0b116a"),sQuery(id+"F3.wireOp",EDGE,"a0615e06-0a48-4c65-8818-f0f693937022"),sQuery(id+"F3.wireOp",EDGE,"08389002-1ce8-438a-b5a4-698ca33590c2"),sQuery(id+"F3.wireOp",EDGE,"1756e4aa-c30a-461e-962c-81ee35d31e55"),sQuery(id+"F3.wireOp",EDGE,"5f84c249-07ea-4efb-9be3-ca494937f772"),sQuery(id+"F3.wireOp",EDGE,"cbefd041-b54f-4587-87b6-437b2290d1fc"),sQuery(id+"F3.wireOp",EDGE,"d44f58d4-f1a7-4aec-b016-8e7f1e498aeb"),sQuery(id+"F3.wireOp",EDGE,"0a5be90b-7545-44ea-9f2d-c726a5a2121c"),sQuery(id+"F3.wireOp",EDGE,"0cfaa442-d102-4580-8ef6-489f2aa1e6b3")])]});
            var Q2;
            Q2=makeQuery(id+"F4.opExtrude","SWEPT_BODY",BODY,{"disambiguationData":[OSD([sQuery(id+"F3.wireOp",EDGE,"9cc7aec6-4d94-4577-ab6c-32f5aa316238"),sQuery(id+"F3.wireOp",EDGE,"5ab2d840-4a32-405a-8c4b-a8126e3e1bc1"),sQuery(id+"F3.wireOp",EDGE,"56de48b4-9620-4637-8196-310e2641530f"),sQuery(id+"F3.wireOp",EDGE,"55327826-e64b-4830-85f2-3f22d36f43b5"),sQuery(id+"F3.wireOp",EDGE,"0245b46f-a639-4a95-8ca3-1568736ceed2"),sQuery(id+"F3.wireOp",EDGE,"9bd8a002-6ca7-4c84-8984-a620eefad103"),sQuery(id+"F3.wireOp",EDGE,"d4736c5e-da0b-46a0-ba9d-17ae07bb2b66"),sQuery(id+"F3.wireOp",EDGE,"125695b8-77e6-4e99-8f78-5f8fae1a0c71"),sQuery(id+"F3.wireOp",EDGE,"c9f25b10-a495-4684-8f25-8f255fabab6e"),sQuery(id+"F3.wireOp",EDGE,"0dbee67a-2ab6-4abb-ae16-0fe64d623848"),sQuery(id+"F3.wireOp",EDGE,"92c08d8e-ed2e-41a3-9c1a-b5ddaf8a0bf1"),sQuery(id+"F3.wireOp",EDGE,"00fabb15-0c1e-492e-85c1-17390e5b12bc"),sQuery(id+"F3.wireOp",EDGE,"065a9352-dddb-4e3f-b02a-444c867b75fe"),sQuery(id+"F3.wireOp",EDGE,"ef206bb6-e4f2-4189-9fc7-a7823c329ad6"),sQuery(id+"F3.wireOp",EDGE,"7199cbbe-c9bf-4cb9-b928-2ff8a84eb09e"),sQuery(id+"F3.wireOp",EDGE,"17bf9ed1-b881-4f74-816d-3511b6b328c7"),sQuery(id+"F3.wireOp",EDGE,"e5b615d0-4193-495d-b285-bd69ae30f000"),sQuery(id+"F3.wireOp",EDGE,"cfeaf62f-6be1-426b-9732-01e1a667be7e"),sQuery(id+"F3.wireOp",EDGE,"ac56344b-5ee6-4fa5-8e47-65b2a4ea3a01"),sQuery(id+"F3.wireOp",EDGE,"45b5fa53-15fd-43a0-91b0-943cc3286fc9")])]});
            var Q3;
            Q3=makeQuery(id+"F4.opExtrude","SWEPT_BODY",BODY,{"disambiguationData":[OSD([sQuery(id+"F3.wireOp",EDGE,"7bdfe37d-9957-4663-8239-5490fd3220d9"),sQuery(id+"F3.wireOp",EDGE,"6a91314f-c002-4565-bbf8-bb9f29165fb8"),sQuery(id+"F3.wireOp",EDGE,"b69f99c7-a6d0-4d1b-8752-9e82ab4c99ec"),sQuery(id+"F3.wireOp",EDGE,"c928f899-12af-4b01-b412-b3b7da3d830f"),sQuery(id+"F3.wireOp",EDGE,"ffa58721-cdd5-406d-be26-d96f7a050df4"),sQuery(id+"F3.wireOp",EDGE,"02fc7fb8-293b-44ff-ab78-63506d0aedb9"),sQuery(id+"F3.wireOp",EDGE,"147fb6cb-2565-4fb5-9280-6afbf9eef36b"),sQuery(id+"F3.wireOp",EDGE,"2cee3704-4124-415a-b391-31af1cf305d7"),sQuery(id+"F3.wireOp",EDGE,"32b2fb71-03c8-4978-9d95-2b5aaf044d0d"),sQuery(id+"F3.wireOp",EDGE,"e5d05796-7d6c-4350-8a4e-d55f5ade2f77"),sQuery(id+"F3.wireOp",EDGE,"77b1164c-8dd4-4680-b616-ac151a422eb2"),sQuery(id+"F3.wireOp",EDGE,"ec0798b8-0fbb-49ea-9766-39d2ee0936b0"),sQuery(id+"F3.wireOp",EDGE,"c4af6478-2a03-47a6-862f-c0c71886b8a3"),sQuery(id+"F3.wireOp",EDGE,"1912a38f-fa28-45c6-ab33-84cac2787056"),sQuery(id+"F3.wireOp",EDGE,"5d79fa95-f66d-4d2b-923b-4d54735f1fbd"),sQuery(id+"F3.wireOp",EDGE,"2db7aef4-a710-4bcf-9c1c-a8a87719953d"),sQuery(id+"F3.wireOp",EDGE,"183449de-345c-4115-9bca-43a403e62dbd"),sQuery(id+"F3.wireOp",EDGE,"e3ac8c9b-cab5-44b0-ad81-0e2b680c384a"),sQuery(id+"F3.wireOp",EDGE,"92e85db6-f458-41f6-a9a1-1e1a1a7e7809"),sQuery(id+"F3.wireOp",EDGE,"f0dbb46f-43a9-447b-9c75-8dfc9b95470d"),sQuery(id+"F3.wireOp",EDGE,"4b73f5f6-f769-4414-bdba-7d253e58fff4"),sQuery(id+"F3.wireOp",EDGE,"a88669dc-35b3-46bb-964f-c9bf6c4ab898"),sQuery(id+"F3.wireOp",EDGE,"2c559bae-f38f-4377-91e6-3c9de70acf11"),sQuery(id+"F3.wireOp",EDGE,"c1caf99b-adaa-42fe-a319-8cbcd819cf89"),sQuery(id+"F3.wireOp",EDGE,"54b04dd4-0ec4-4956-b19c-1141095738e3"),sQuery(id+"F3.wireOp",EDGE,"098f7a84-b7b8-4879-b21a-5c38879e4110"),sQuery(id+"F3.wireOp",EDGE,"b406a8e6-a226-4f3d-ac30-e4d06e4dac62"),sQuery(id+"F3.wireOp",EDGE,"36f95d1d-68ce-4231-ad71-3960c85e5915"),sQuery(id+"F3.wireOp",EDGE,"dc12cad8-2eed-454e-aa74-30099b1c9064"),sQuery(id+"F3.wireOp",EDGE,"4c78a4fd-cd81-43d6-85d6-6e4d3fbc1e98"),sQuery(id+"F3.wireOp",EDGE,"ee9e30de-787b-4e8f-b425-43a8e9289f81"),sQuery(id+"F3.wireOp",EDGE,"2518a3a4-c96b-4463-8704-0b71c65c60d2"),sQuery(id+"F3.wireOp",EDGE,"c9129a67-398c-4e37-92cb-2d54ff2e2e82"),sQuery(id+"F3.wireOp",EDGE,"d429d547-9f5b-42c6-bcca-effad2fa908f"),sQuery(id+"F3.wireOp",EDGE,"99d16e94-b2b3-43d5-9c7b-7bd463994dcb"),sQuery(id+"F3.wireOp",EDGE,"32993909-9a70-47ee-9097-89fff220f839"),sQuery(id+"F3.wireOp",EDGE,"6eabbeed-9496-4825-b168-63782a34f495"),sQuery(id+"F3.wireOp",EDGE,"f74987e3-8e60-4a5b-857f-839ae8aaf0cf"),sQuery(id+"F3.wireOp",EDGE,"1c218c86-035d-4441-93c0-9621d3297c3a"),sQuery(id+"F3.wireOp",EDGE,"0133f513-4b11-4cc4-b075-4625e9591e41"),sQuery(id+"F3.wireOp",EDGE,"fe921ad4-a8f5-4772-9aeb-350aca2e8948"),sQuery(id+"F3.wireOp",EDGE,"bfde0a4f-3cec-4f8e-8a23-dd1441b34c2b"),sQuery(id+"F3.wireOp",EDGE,"b41521ff-c5df-4b64-83ed-5e7635cf4438"),sQuery(id+"F3.wireOp",EDGE,"ed692599-6bbb-4379-8e89-ea326a0a0f87"),sQuery(id+"F3.wireOp",EDGE,"a98451c0-d76c-436e-99f9-a3fe9c8430a4"),sQuery(id+"F3.wireOp",EDGE,"561965b2-3050-4f49-9305-d98a2b852bbe"),sQuery(id+"F3.wireOp",EDGE,"e13dfa59-48e6-4b4e-94b9-1fc5254b0f2e"),sQuery(id+"F3.wireOp",EDGE,"0354e106-253a-4bfa-b5b7-b09cd0f2f6c0"),sQuery(id+"F3.wireOp",EDGE,"8df1dcc8-d00a-4777-85fd-8af8e9830bd1"),sQuery(id+"F3.wireOp",EDGE,"26ce3762-0d1a-4b81-9a23-debcfc24da1c"),sQuery(id+"F3.wireOp",EDGE,"3e900f8f-3ffb-4e32-b536-61fea2f3e30a"),sQuery(id+"F3.wireOp",EDGE,"4a1b5445-5559-461f-b6f1-b4cd9b95ea10")])]});
            var Q4;
            Q4=makeQuery(id+"F1.opRevolve","SWEPT_BODY",BODY,{"disambiguationData":[OSD([sQuery(id+"F0.wireOp",EDGE,"E0"),sQuery(id+"F0.wireOp",EDGE,"E1")])]});
            var Q5;
            Q5=qCreatedBy(makeId("Origin.pointOp"),VERTEX);
            transform(context, id + "F5", {"entities" : qUnion([Q0, Q1, Q2, Q3, Q4]), "transformType" : TransformType.SCALE_UNIFORMLY, "scale" : 0.03, "scalePoint" : qUnion([Q5]), "makeCopy" : false});
        }
        {
            var Q0;
            Q0=qCreatedBy(makeId("Top.planeOp"),FACE);
            var sketch = newSketch(context, id + "F6", { "sketchPlane" : qUnion([Q0])});
            skLineSegment(sketch, "E270", {"start": v(0, 15) * mm, "end": v(0, -15) * mm});
            skArc(sketch, "E271", {"start": v(0, 15) * mm, "mid": v(-15, 0) * mm, "end": v(0, -15) * mm});
            skArc(sketch, "E272", {"start": v(0, 10.25) * mm, "mid": v(-10.25, 0) * mm, "end": v(0, -10.25) * mm});
            skArc(sketch, "E273", {"start": v(0, 7) * mm, "mid": v(-7, 0) * mm, "end": v(0, -7) * mm});
            skSolve(sketch);
        }
        {
            var Q0;
            {var subQ0=sQuery(id+"F6.wireOp",EDGE,"E271");Q0=makeQuery(id+"F6.imprint","IMPRINT",FACE,{"disambiguationData":[TD([[makeQuery(id+"F6.imprint","IMPRINT",EDGE,{"derivedFrom":subQ0}),1.0]])]});}
            var Q1;
            {var subQ0=sQuery(id+"F6.wireOp",EDGE,"E273");Q1=makeQuery(id+"F6.imprint","IMPRINT",FACE,{"disambiguationData":[TD([[makeQuery(id+"F6.imprint","IMPRINT",EDGE,{"derivedFrom":subQ0}),1.0]])]});}
            var Q2;
            Q2=sQuery(id+"F6.wireOp",EDGE,"E270");
            revolve(context, id + "F7", {"operationType" : NewBodyOperationType.REMOVE, "entities" : qUnion([Q0, Q1]), "axis" : qUnion([Q2]), "revolveType" : RevolveType.FULL});
        }
        {
            var Q0;
            Q0=makeQuery(id+"F1.opRevolve","SWEPT_BODY",BODY,{"disambiguationData":[OSD([sQuery(id+"F0.wireOp",EDGE,"E0"),sQuery(id+"F0.wireOp",EDGE,"E1")])]});
            var Q1;
            Q1=sQuery(id+"F0.wireOp",VERTEX,"E1.center");
            transform(context, id + "F8", {"entities" : qUnion([Q0]), "transformType" : TransformType.SCALE_UNIFORMLY, "scale" : 1.4, "scalePoint" : qUnion([Q1]), "makeCopy" : false});
        }
        {
            var Q0;
            Q0=qCreatedBy(makeId("Front.planeOp"),FACE);
            var sketch = newSketch(context, id + "F9", { "sketchPlane" : qUnion([Q0])});
            skCircle(sketch, "E274", {"center": v(0, -5.12) * mm, "radius": 2 * mm});
            skSolve(sketch);
        }
        {
            var Q0;
            Q0=qSketchRegion(id+"F9",true);
            extrude(context, id + "F10", {"entities" : qUnion([Q0]), "operationType" : NewBodyOperationType.REMOVE, "oppositeDirection" : true, "depth" : 25 * mm});
        }
        {
            var Q0;
            Q0=qCreatedBy(makeId("Top.planeOp"),FACE);
            var sketch = newSketch(context, id + "F11", { "sketchPlane" : qUnion([Q0])});
            skLineSegment(sketch, "E275", {"start": v(-53.08, 0) * mm, "end": v(57.3, 0) * mm});
            skArc(sketch, "E276", {"start": v(-14.25, 0) * mm, "mid": v(0, 14.25) * mm, "end": v(14.25, 0) * mm});
            skSolve(sketch);
        }
        {
            var Q0;
            Q0=sQuery(id+"F11.wireOp",EDGE,"E275");
            cPlane(context, id + "F12", {"entities" : qUnion([Q0]), "cplaneType" : CPlaneType.LINE_ANGLE, "offset" : 25 * mm, "angle" : 40 * degree, "width" : 150 * mm, "height" : 150 * mm});
        }
        {
            var Q0;
            Q0=qCreatedBy(id+"F12.planeOp",FACE);
            var sketch = newSketch(context, id + "F13", { "sketchPlane" : qUnion([Q0])});
            skText(sketch, "E277", { "text": "using", "fontName": "OpenSans-Italic.ttf"});
            const initialGuessF13  = {"E277": [-0.00677, -0.003, 1, 0, 0.004]};
            skSetInitialGuess(sketch, initialGuessF13);
            skSolve(sketch);
        }
        {
            var Q0;
            Q0=sQuery(id+"F11.wireOp",EDGE,"E276");
            var Q1;
            Q1=sQuery(id+"F11.wireOp",EDGE,"E275");
            revolve(context, id + "F14", {"bodyType" : ToolBodyType.SURFACE, "surfaceEntities" : qUnion([Q0]), "axis" : qUnion([Q1]), "revolveType" : RevolveType.FULL});
        }
        {
            var Q0;
            Q0 = qSketchRegion(id + "F13", true);
            var Q1;
            Q1=makeQuery(id+"F14.opRevolve","SWEPT_FACE",FACE,{"disambiguationData":[OSD([sQuery(id+"F11.wireOp",EDGE,"E276")])]});
            extrude(context, id + "F15", {"entities" : qUnion([Q0]), "operationType" : NewBodyOperationType.ADD, "endBound" : BoundingType.UP_TO_SURFACE, "depth" : 25 * mm, "endBoundEntityFace" : qUnion([Q1]), "offsetDistance" : 25 * mm});
        }
    });
